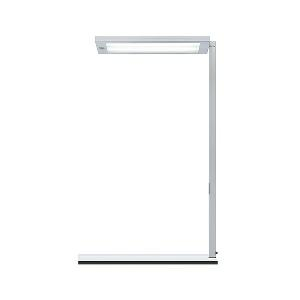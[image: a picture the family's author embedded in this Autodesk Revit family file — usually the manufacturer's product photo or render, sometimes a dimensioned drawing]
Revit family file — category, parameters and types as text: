
# Revit family: lavigo_-_dpt_12000_840_r_g2_00804497_4725
name_source: partatom
category: Lighting Fixtures
units: mm (PartAtom-declared; Revit-internal decimal feet)

## family parameters
Cut with Voids When Loaded = No
Host = Face
Light Source = No
Part Type = Normal
Room Calculation Point = No
Round Connector Dimension = Use Diameter
Shared = No

## types (1)
- LAVIGO - DPT 12000/840/R/G2 (1 x LED, 11650 lm, 4000K)
    Apparent Load = 77 VA
    Approval mark = CE
    CIE Flux Codes = 60 87 97 15 100
    Color Rendering = 80-89
    Color Temperature = 4000K
    Control Gear = Electronic ballast
    Default Elevation = 1800 mm
    Description = DPT 12000/840/R/G2|Desk-mounted luminaire|light source: LED|work equipment: Electronic ballast|connected load: 220-240 V, 50/60 Hz|Power consumption: approx. 77 W|standby: approx. 0,50|power factor: approx. 0,930|luminous flux: 11650 lm|luminous efficacy: 151 lm/W|light distribution: Direct/indirect|direct ratio: approx. 15 %|colour temperature: Cold white, ca. 4000 K|color rendering index (CRI): >= 80|chromaticity tolerance:  3 SDCM|technology: Presence and daylight sensor control (PIR)|operation: Multi-function switch|luminaire body|material: Steel/plastic|surface: Painted|colour: White|lamp cover: Acrylic (PMMA), Satine|tubular section|material: Steel tube|surface: Painted|Form: Tubular section upright|colour of tubular section: White|weight (net): approx. 9.5 kg|mains lead: 3.70 m Mains plug CEE 7/VII|Fastening: Socket, Table adaptor|decorative contrast side parts: Flint grey|glare control: Prism aperture|luminance(L65): <= 3000 cd/m|unified glare rating(4H 8H): <=  16|special features: Luminaire head detachable, Cradle to Cradle Certified TM, Direct light component with edge light and light-guide technology for homogenous light exit, Flicker-free, Integrated light and presence sensor PIR, Retrofittable with TALK module, Inclination of tubular section adjustable, Separated, direct and indirect light individually adjustable|Approval mark: VDE - ENEC|
    Frequency = 50 Hz, 60 Hz
    Height = 36 mm
    Lamp = 1 x LED
    Lamp Light Flux = 11650 lm
    Lamp count = 1
    Length = 675 mm
    Luminous efficacy = 151 lm/W
    Manufacturer = Waldmann
    ModVariant = No
    Model = 00804497
    Mounting Place = Table
    Mounting Type = Surface mounted
    Number of Poles = 1
    OnlyDefault = Yes
    Power Factor = 1
    Product Name = LAVIGO - DPT 12000/840/R/G2
    Product group = Desk mounted luminaire with detector
    ProductGroupID = 2201
    Protection Class = Protection class I
    Protection Degree = IP 20
    RLX_Detail_Level = 1
    RLX_Emergency_Light_Flux = 0 lm
    RLX_Emergency_Type = 0
    RLX_Emergency_Type_DB = No
    RlxData = <blob elided: 35629 chars, md5=b619464a>
    Socket = socket
    Standby Power = 0 W
    System Light Flux = 11650 lm
    System Power = 77 W
    Type Comments = Product without accessories
    Type Image = 121716000-00630762.jpg
    URL = http://relux.com
    VarID = ---
    Voltage = 230 V
    Voltage Range = 220-240 V
    Weight = 0.00 kg
    Width = 320 mm

## geometry (parser evidence)
native form markers: Blend x4, Sweep x13
no freeform markers — native parametric forms only
